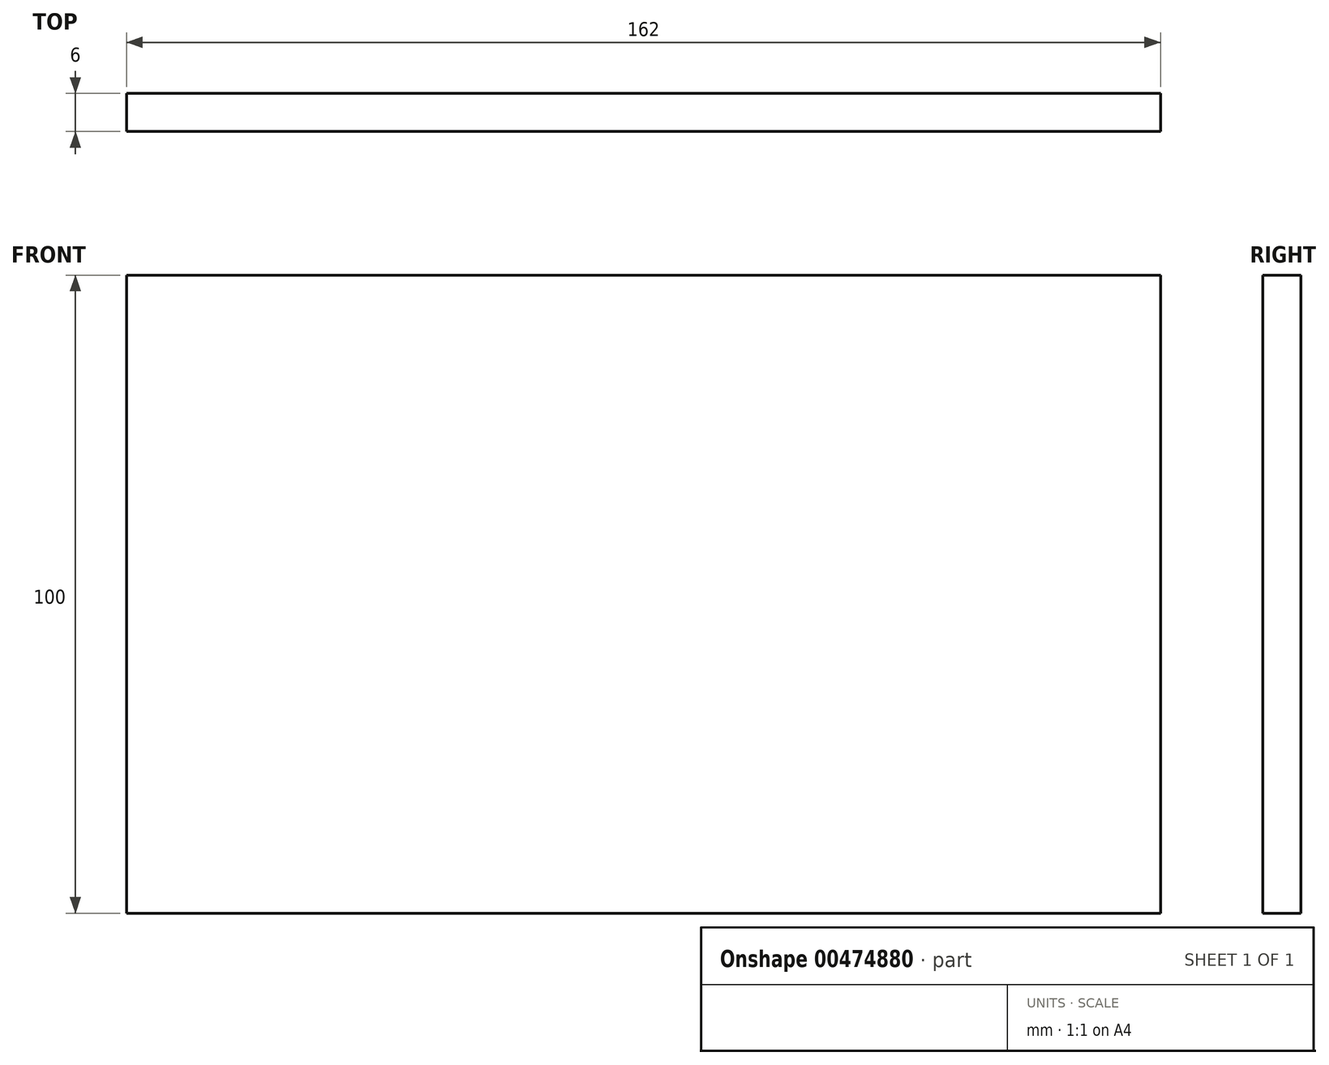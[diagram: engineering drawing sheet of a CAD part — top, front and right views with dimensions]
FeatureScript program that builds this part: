
annotation { "Feature Type Name" : "Feature", "Feature Type Description" : "" }
export const myFeature = defineFeature(function(context is Context, id is Id, definition is map)
    precondition{}
    {
        {
            var Q0;
            Q0=qCreatedBy(makeId("Front.planeOp"),FACE);
            var sketch = newSketch(context, id + "F0", { "sketchPlane" : qUnion([Q0])});
            skLineSegment(sketch, "E0.bottom", {"start": v(81, -50) * mm, "end": v(-81, -50) * mm});
            skLineSegment(sketch, "E0.top", {"start": v(81, 50) * mm, "end": v(-81, 50) * mm});
            skLineSegment(sketch, "E0.left", {"start": v(81, -50) * mm, "end": v(81, 50) * mm});
            skLineSegment(sketch, "E0.right", {"start": v(-81, -50) * mm, "end": v(-81, 50) * mm});
            skPoint(sketch, "E0.middle", {"position": v(0, 0) * mm});
            skSolve(sketch);
        }
        {
            var Q0;
            Q0=qSketchRegion(id+"F0",true);
            extrude(context, id + "F1", {"entities" : qUnion([Q0]), "endBound" : BoundingType.SYMMETRIC, "depth" : 6 * mm});
        }
    });
